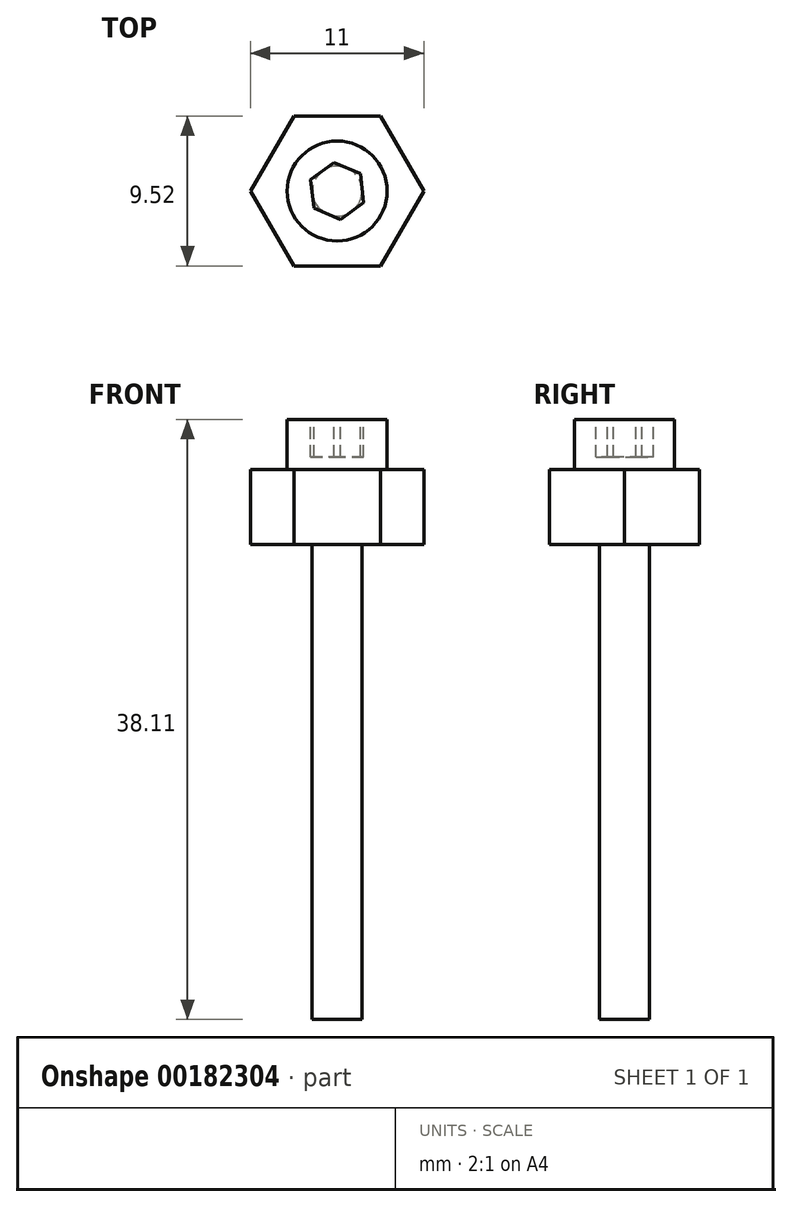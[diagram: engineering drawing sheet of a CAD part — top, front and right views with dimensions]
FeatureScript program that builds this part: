
annotation { "Feature Type Name" : "Feature", "Feature Type Description" : "" }
export const myFeature = defineFeature(function(context is Context, id is Id, definition is map)
    precondition{}
    {
        {
            var Q0;
            Q0=qCreatedBy(makeId("Top.planeOp"),FACE);
            var sketch = newSketch(context, id + "F0", { "sketchPlane" : qUnion([Q0])});
            skCircle(sketch, "E0.cCircle", {"center": v(0, 0) * mm, "radius": 4.76 * mm, "construction": true});
            skLineSegment(sketch, "E0.0", {"start": v(2.75, -4.76) * mm, "end": v(-2.75, -4.76) * mm});
            skLineSegment(sketch, "E0.1", {"start": v(-2.75, -4.76) * mm, "end": v(-5.5, 0) * mm});
            skLineSegment(sketch, "E0.2", {"start": v(-5.5, 0) * mm, "end": v(-2.75, 4.76) * mm});
            skLineSegment(sketch, "E0.3", {"start": v(-2.75, 4.76) * mm, "end": v(2.75, 4.76) * mm});
            skLineSegment(sketch, "E0.4", {"start": v(2.75, 4.76) * mm, "end": v(5.5, 0) * mm});
            skLineSegment(sketch, "E0.5", {"start": v(5.5, 0) * mm, "end": v(2.75, -4.76) * mm});
            skPoint(sketch, "E0.0.midPoint", {"position": v(0, -4.76) * mm});
            skCircle(sketch, "E1", {"center": v(0, 0) * mm, "radius": 1.59 * mm});
            skSolve(sketch);
        }
        {
            var Q0;
            Q0 = qSketchRegion(id + "F0", true);
            extrude(context, id + "F1", {"entities" : qUnion([Q0]), "oppositeDirection" : true, "depth" : 4.76 * mm});
        }
        {
            var Q0;
            Q0=qCreatedBy(makeId("Top.planeOp"),FACE);
            var sketch = newSketch(context, id + "F2", { "sketchPlane" : qUnion([Q0])});
            skCircle(sketch, "E2", {"center": v(0, 0) * mm, "radius": 3.18 * mm});
            skPoint(sketch, "E3.0.midPoint", {"position": v(1.59, 0) * mm});
            skSolve(sketch);
        }
        {
            var Q0;
            Q0=makeQuery(id+"F2.imprint","IMPRINT",FACE,{"disambiguationData":[TD([[makeQuery(id+"F2.imprint","IMPRINT",EDGE,{"derivedFrom":sQuery(id+"F2.wireOp",EDGE,"E2")}),1.0]])]});
            extrude(context, id + "F3", {"entities" : qUnion([Q0]), "depth" : 3.17 * mm});
        }
        {
            var Q0;
            Q0=makeQuery(id+"F3.opExtrude","CAP_FACE",FACE,{"disambiguationData":[OSD([sQuery(id+"F2.wireOp",EDGE,"E2"),sQuery(id+"F2.wireOp",EDGE,"E3.0"),sQuery(id+"F2.wireOp",EDGE,"E3.1"),sQuery(id+"F2.wireOp",EDGE,"E3.2"),sQuery(id+"F2.wireOp",EDGE,"E3.3"),sQuery(id+"F2.wireOp",EDGE,"E3.4"),sQuery(id+"F2.wireOp",EDGE,"E3.5")])],"isStart":true});
            var sketch = newSketch(context, id + "F4", { "sketchPlane" : qUnion([Q0])});
            skCircle(sketch, "E4", {"center": v(0, 0) * mm, "radius": 1.59 * mm});
            skSolve(sketch);
        }
        {
            var Q0;
            Q0 = qSketchRegion(id + "F4", true);
            extrude(context, id + "F5", {"entities" : qUnion([Q0]), "depth" : 34.92 * mm});
        }
        {
            var Q0;
            Q0=makeQuery(id+"F3.opExtrude","CAP_FACE",FACE,{"disambiguationData":[OSD([sQuery(id+"F2.wireOp",EDGE,"E2")])],"isStart":false});
            var sketch = newSketch(context, id + "F6", { "sketchPlane" : qUnion([Q0])});
            skCircle(sketch, "E5.cCircle", {"center": v(0, 0) * mm, "radius": 1.59 * mm, "construction": true});
            skLineSegment(sketch, "E5.0", {"start": v(-1.4, -1.18) * mm, "end": v(-1.73, 0.62) * mm});
            skLineSegment(sketch, "E5.1", {"start": v(-1.73, 0.62) * mm, "end": v(-0.33, 1.8) * mm});
            skLineSegment(sketch, "E5.2", {"start": v(-0.33, 1.8) * mm, "end": v(1.4, 1.18) * mm});
            skLineSegment(sketch, "E5.3", {"start": v(1.4, 1.18) * mm, "end": v(1.73, -0.62) * mm});
            skLineSegment(sketch, "E5.4", {"start": v(1.73, -0.62) * mm, "end": v(0.33, -1.8) * mm});
            skLineSegment(sketch, "E5.5", {"start": v(0.33, -1.8) * mm, "end": v(-1.4, -1.18) * mm});
            skPoint(sketch, "E5.0.midPoint", {"position": v(-1.56, -0.28) * mm});
            skSolve(sketch);
        }
        {
            var Q0;
            Q0=makeQuery(id+"F6.imprint","IMPRINT",FACE,{"disambiguationData":[TD([[makeQuery(id+"F6.imprint","IMPRINT",EDGE,{"derivedFrom":sQuery(id+"F6.wireOp",EDGE,"E5.0")}),-1.0]])]});
            extrude(context, id + "F7", {"entities" : qUnion([Q0]), "operationType" : NewBodyOperationType.ADD, "oppositeDirection" : true, "depth" : 3.05 * mm});
        }
        {
            var Q0;
            Q0=makeQuery(id+"F3.opExtrude","CAP_FACE",FACE,{"disambiguationData":[OSD([sQuery(id+"F2.wireOp",EDGE,"E2")])],"isStart":false});
            var sketch = newSketch(context, id + "F8", { "sketchPlane" : qUnion([Q0])});
            skCircle(sketch, "E6.cCircle", {"center": v(0, 0) * mm, "radius": 1.59 * mm, "construction": true});
            skLineSegment(sketch, "E6.0", {"start": v(1.54, -1) * mm, "end": v(-0.09, -1.83) * mm});
            skLineSegment(sketch, "E6.1", {"start": v(-0.09, -1.83) * mm, "end": v(-1.63, -0.84) * mm});
            skLineSegment(sketch, "E6.2", {"start": v(-1.63, -0.84) * mm, "end": v(-1.54, 1) * mm});
            skLineSegment(sketch, "E6.3", {"start": v(-1.54, 1) * mm, "end": v(0.09, 1.83) * mm});
            skLineSegment(sketch, "E6.4", {"start": v(0.09, 1.83) * mm, "end": v(1.63, 0.84) * mm});
            skLineSegment(sketch, "E6.5", {"start": v(1.63, 0.84) * mm, "end": v(1.54, -1) * mm});
            skPoint(sketch, "E6.0.midPoint", {"position": v(0.73, -1.41) * mm});
            skSolve(sketch);
        }
        {
            var Q0;
            Q0 = qSketchRegion(id + "F8", true);
            extrude(context, id + "F9", {"entities" : qUnion([Q0]), "operationType" : NewBodyOperationType.REMOVE, "oppositeDirection" : true, "depth" : 3.17 * mm});
        }
        {
            var Q0;
            Q0=makeQuery(id+"F3.opExtrude","SWEPT_BODY",BODY,{"disambiguationData":[OSD([sQuery(id+"F2.wireOp",EDGE,"E2")])]});
            deleteBodies(context, id + "F10", {"entities" : qUnion([Q0])});
        }
        {
            var Q0;
            Q0=makeQuery(id+"F5.opExtrude","CAP_FACE",FACE,{"disambiguationData":[OSD([sQuery(id+"F4.wireOp",EDGE,"E4")])],"isStart":true});
            var sketch = newSketch(context, id + "F11", { "sketchPlane" : qUnion([Q0])});
            skCircle(sketch, "E7.cCircle", {"center": v(0, 0) * mm, "radius": 4.76 * mm, "construction": true});
            skLineSegment(sketch, "E7.0", {"start": v(1.8, 5.2) * mm, "end": v(5.4, 1.04) * mm});
            skLineSegment(sketch, "E7.1", {"start": v(5.4, 1.04) * mm, "end": v(3.6, -4.16) * mm});
            skLineSegment(sketch, "E7.2", {"start": v(3.6, -4.16) * mm, "end": v(-1.8, -5.2) * mm});
            skLineSegment(sketch, "E7.3", {"start": v(-1.8, -5.2) * mm, "end": v(-5.4, -1.04) * mm});
            skLineSegment(sketch, "E7.4", {"start": v(-5.4, -1.04) * mm, "end": v(-3.6, 4.16) * mm});
            skLineSegment(sketch, "E7.5", {"start": v(-3.6, 4.16) * mm, "end": v(1.8, 5.2) * mm});
            skPoint(sketch, "E7.0.midPoint", {"position": v(3.6, 3.12) * mm});
            skCircle(sketch, "E8", {"center": v(0, 0) * mm, "radius": 1.59 * mm});
            skSolve(sketch);
        }
        {
            var Q0;
            Q0 = qSketchRegion(id + "F11", true);
            extrude(context, id + "F12", {"entities" : qUnion([Q0]), "depth" : 25.4 * mm});
        }
        {
            var Q0;
            Q0=makeQuery(id+"F5.opExtrude","SWEPT_BODY",BODY,{"disambiguationData":[OSD([sQuery(id+"F4.wireOp",EDGE,"E4")])]});
            var Q1;
            Q1=makeQuery(id+"F12.opExtrude","SWEPT_BODY",BODY,{"disambiguationData":[OSD([sQuery(id+"F11.wireOp",EDGE,"E7.0"),sQuery(id+"F11.wireOp",EDGE,"E7.1"),sQuery(id+"F11.wireOp",EDGE,"E7.2"),sQuery(id+"F11.wireOp",EDGE,"E7.3"),sQuery(id+"F11.wireOp",EDGE,"E7.4"),sQuery(id+"F11.wireOp",EDGE,"E7.5"),sQuery(id+"F11.wireOp",EDGE,"E8")])]});
            deleteBodies(context, id + "F13", {"entities" : qUnion([Q0, Q1])});
        }
        {
            var Q0;
            Q0=qCreatedBy(makeId("Top.planeOp"),FACE);
            var sketch = newSketch(context, id + "F14", { "sketchPlane" : qUnion([Q0])});
            skCircle(sketch, "E9", {"center": v(0, 0) * mm, "radius": 3.18 * mm});
            skSolve(sketch);
        }
        {
            var Q0;
            Q0 = qSketchRegion(id + "F14", true);
            extrude(context, id + "F15", {"entities" : qUnion([Q0]), "depth" : 3.17 * mm});
        }
        {
            var Q0;
            Q0=makeQuery(id+"F15.opExtrude","CAP_FACE",FACE,{"disambiguationData":[OSD([sQuery(id+"F14.wireOp",EDGE,"E9")])],"isStart":true});
            var sketch = newSketch(context, id + "F16", { "sketchPlane" : qUnion([Q0])});
            skCircle(sketch, "E10", {"center": v(0, 0) * mm, "radius": 1.59 * mm});
            skSolve(sketch);
        }
        {
            var Q0;
            Q0 = qSketchRegion(id + "F16", true);
            extrude(context, id + "F17", {"entities" : qUnion([Q0]), "operationType" : NewBodyOperationType.ADD, "depth" : 34.92 * mm});
        }
        {
            var Q0;
            Q0=makeQuery(id+"F15.opExtrude","CAP_FACE",FACE,{"disambiguationData":[OSD([sQuery(id+"F14.wireOp",EDGE,"E9")])],"isStart":false});
            var sketch = newSketch(context, id + "F18", { "sketchPlane" : qUnion([Q0])});
            skCircle(sketch, "E11.cCircle", {"center": v(0, 0) * mm, "radius": 1.59 * mm, "construction": true});
            skLineSegment(sketch, "E11.0", {"start": v(-1.68, 0.72) * mm, "end": v(-0.22, 1.82) * mm});
            skLineSegment(sketch, "E11.1", {"start": v(-0.22, 1.82) * mm, "end": v(1.47, 1.1) * mm});
            skLineSegment(sketch, "E11.2", {"start": v(1.47, 1.1) * mm, "end": v(1.68, -0.72) * mm});
            skLineSegment(sketch, "E11.3", {"start": v(1.68, -0.72) * mm, "end": v(0.22, -1.82) * mm});
            skLineSegment(sketch, "E11.4", {"start": v(0.22, -1.82) * mm, "end": v(-1.47, -1.1) * mm});
            skLineSegment(sketch, "E11.5", {"start": v(-1.47, -1.1) * mm, "end": v(-1.68, 0.72) * mm});
            skPoint(sketch, "E11.0.midPoint", {"position": v(-0.95, 1.27) * mm});
            skSolve(sketch);
        }
        {
            var Q0;
            Q0=makeQuery(id+"F18.imprint","IMPRINT",FACE,{"disambiguationData":[TD([[makeQuery(id+"F18.imprint","IMPRINT",EDGE,{"derivedFrom":sQuery(id+"F18.wireOp",EDGE,"E11.0")}),-1.0]])]});
            extrude(context, id + "F19", {"entities" : qUnion([Q0]), "operationType" : NewBodyOperationType.REMOVE, "oppositeDirection" : true, "depth" : 2.38 * mm});
        }
    });
